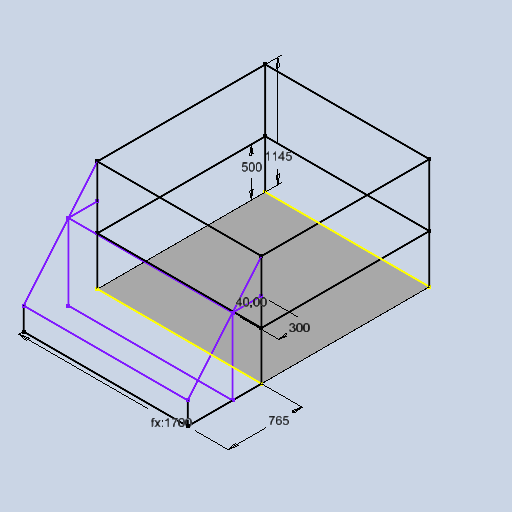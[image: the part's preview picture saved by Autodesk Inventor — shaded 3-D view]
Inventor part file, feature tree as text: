
AUTODESK INVENTOR PART (.ipt)
format: ipt  version: 2025 (Build 290162010, 162A)  size: 124,416 bytes
history: native  units: mm
features: sketch x2, extrude x1
ambient origin geometry x8: Origin, YZ Plane, XZ Plane, XY Plane, X Axis, Y Axis, Z Axis, Center Point
bodies: Solid1 (feature_tree)
feature tree (3):
  extrude  "Extrusion1"  Depth=1740.0mm
  sketch  "3D Sketch1"
  sketch  "Sketch1"  dims[d0=1700.0mm d1=1740.0mm d2=1.0mm d3=0.0mm d4=1145.0mm d7=500.0mm d8=1700.0mm d14=765.000058mm d15=300.0mm d16=6.981317mm]
